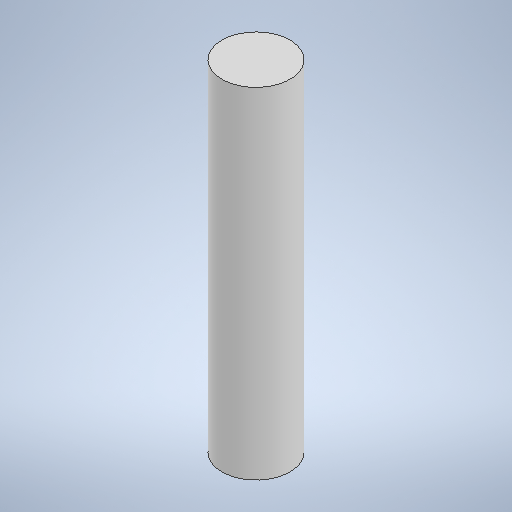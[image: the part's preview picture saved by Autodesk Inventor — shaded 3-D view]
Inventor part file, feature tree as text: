
AUTODESK INVENTOR PART (.ipt)
format: ipt  version: 2025.2 (Build 292293000, 293)  size: 229,376 bytes
history: native  units: mm
features: other x1, extrude x1, sketch x1
ambient origin geometry x8: Origin, YZ Plane, XZ Plane, XY Plane, X Axis, Y Axis, Z Axis, Center Point
bodies: Body1 (feature_tree)
feature tree (3):
  other  "ソリッド1"
  extrude  "押し出し1"  Depth=2.0mm
  sketch  "スケッチ1"
